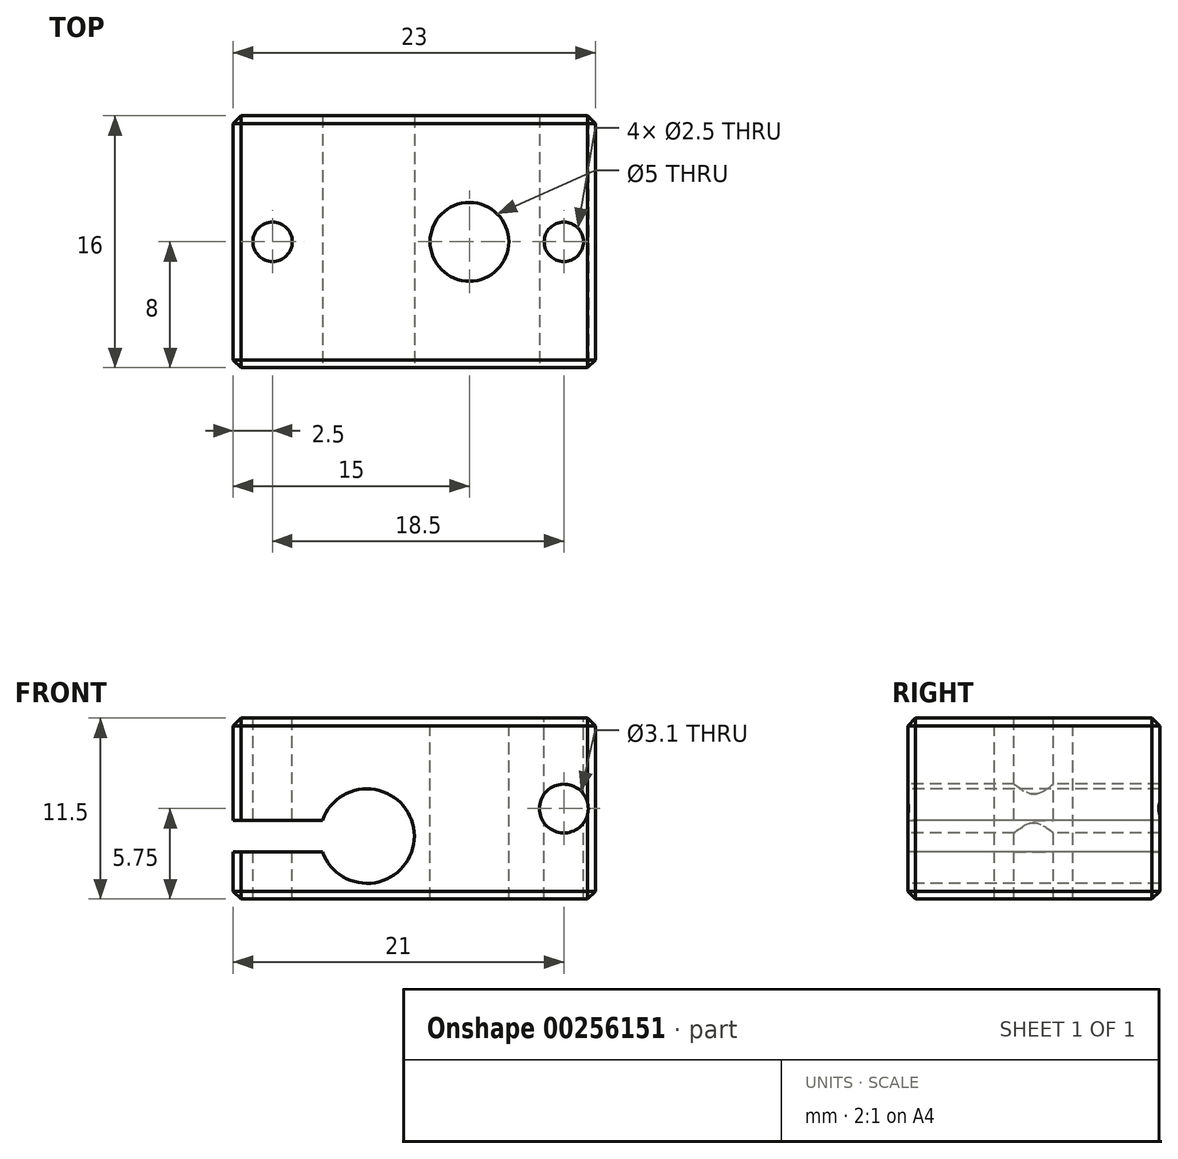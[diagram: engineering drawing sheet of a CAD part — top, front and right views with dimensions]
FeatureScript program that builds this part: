
annotation { "Feature Type Name" : "Feature", "Feature Type Description" : "" }
export const myFeature = defineFeature(function(context is Context, id is Id, definition is map)
    precondition{}
    {
        {
            var Q0;
            Q0=qCreatedBy(makeId("Front.planeOp"),FACE);
            var sketch = newSketch(context, id + "F0", { "sketchPlane" : qUnion([Q0])});
            skLineSegment(sketch, "E0.bottom", {"start": v(-11.5, 5.75) * mm, "end": v(11.5, 5.75) * mm});
            skLineSegment(sketch, "E0.top", {"start": v(-11.5, -5.75) * mm, "end": v(11.5, -5.75) * mm});
            skLineSegment(sketch, "E0.left", {"start": v(-11.5, 5.75) * mm, "end": v(-11.5, -5.75) * mm});
            skLineSegment(sketch, "E0.right", {"start": v(11.5, 5.75) * mm, "end": v(11.5, -5.75) * mm});
            skPoint(sketch, "E0.middle", {"position": v(0, 0) * mm});
            skSolve(sketch);
        }
        {
            var Q0;
            Q0=makeQuery(id+"F0.imprint","IMPRINT",FACE,{"disambiguationData":[TD([[makeQuery(id+"F0.imprint","IMPRINT",EDGE,{"derivedFrom":sQuery(id+"F0.wireOp",EDGE,"E0.bottom")}),-1.0]])]});
            extrude(context, id + "F1", {"entities" : qUnion([Q0]), "endBound" : BoundingType.SYMMETRIC, "depth" : 16 * mm});
        }
        {
            var Q0;
            Q0=makeQuery(id+"F1.opExtrude","CAP_FACE",FACE,{"disambiguationData":[OSD([sQuery(id+"F0.wireOp",EDGE,"E0.bottom"),sQuery(id+"F0.wireOp",EDGE,"E0.top"),sQuery(id+"F0.wireOp",EDGE,"E0.left"),sQuery(id+"F0.wireOp",EDGE,"E0.right")])],"isStart":false});
            var sketch = newSketch(context, id + "F2", { "sketchPlane" : qUnion([Q0])});
            skArc(sketch, "E1", {"start": v(-5.83, -2.75) * mm, "mid": v(0, -1.75) * mm, "end": v(-5.83, -0.75) * mm});
            skCircle(sketch, "E2", {"center": v(9.5, 0) * mm, "radius": 1.55 * mm});
            skLineSegment(sketch, "E3", {"start": v(-5.83, -2.75) * mm, "end": v(-11.5, -2.75) * mm});
            skLineSegment(sketch, "E4", {"start": v(-11.5, -2.75) * mm, "end": v(-11.5, -0.75) * mm});
            skLineSegment(sketch, "E5", {"start": v(-11.5, -0.75) * mm, "end": v(-5.83, -0.75) * mm});
            skSolve(sketch);
        }
        {
            var Q0;
            Q0 = qSketchRegion(id + "F2", true);
            extrude(context, id + "F3", {"entities" : qUnion([Q0]), "operationType" : NewBodyOperationType.REMOVE, "endBound" : BoundingType.UP_TO_NEXT, "oppositeDirection" : true, "depth" : 25 * mm});
        }
        {
            var Q0;
            Q0=makeQuery(id+"F1.opExtrude","SWEPT_FACE",FACE,{"disambiguationData":[OSD([sQuery(id+"F0.wireOp",EDGE,"E0.bottom")])]});
            var sketch = newSketch(context, id + "F4", { "sketchPlane" : qUnion([Q0])});
            skCircle(sketch, "E6", {"center": v(-9, 0) * mm, "radius": 1.25 * mm});
            skCircle(sketch, "E7", {"center": v(3.5, 0) * mm, "radius": 2.5 * mm});
            skCircle(sketch, "E8", {"center": v(9.5, 0) * mm, "radius": 1.25 * mm});
            skSolve(sketch);
        }
        {
            var Q0;
            Q0 = qSketchRegion(id + "F4", true);
            extrude(context, id + "F5", {"entities" : qUnion([Q0]), "operationType" : NewBodyOperationType.REMOVE, "endBound" : BoundingType.THROUGH_ALL, "oppositeDirection" : true, "depth" : 25 * mm});
        }
        {
            var Q0;
            Q0=makeQuery(id+"F1.opExtrude","CAP_EDGE",EDGE,{"disambiguationData":[OSD([sQuery(id+"F0.wireOp",EDGE,"E0.bottom")])],"isStart":false});
            var Q1;
            {var subQ0=sQuery(id+"F0.wireOp",EDGE,"E0.bottom");var subQ1=sQuery(id+"F0.wireOp",EDGE,"E0.left");Q1=makeQuery(id+"F3.boolean.opBoolean","SPLIT",EDGE,{"disambiguationData":[TD([makeQuery(id+"F1.opExtrude","SWEPT_FACE",FACE,{"disambiguationData":[OSD([subQ0])]})])],"derivedFrom":makeQuery(id+"F1.opExtrude","CAP_EDGE",EDGE,{"disambiguationData":[OSD([subQ1])],"isStart":false})});}
            var Q2;
            {var subQ0=sQuery(id+"F0.wireOp",EDGE,"E0.left");var subQ1=sQuery(id+"F0.wireOp",EDGE,"E0.top");Q2=makeQuery(id+"F3.boolean.opBoolean","SPLIT",EDGE,{"disambiguationData":[TD([makeQuery(id+"F1.opExtrude","SWEPT_FACE",FACE,{"disambiguationData":[OSD([subQ1])]})])],"derivedFrom":makeQuery(id+"F1.opExtrude","CAP_EDGE",EDGE,{"disambiguationData":[OSD([subQ0])],"isStart":false})});}
            var Q3;
            Q3=makeQuery(id+"F1.opExtrude","CAP_EDGE",EDGE,{"disambiguationData":[OSD([sQuery(id+"F0.wireOp",EDGE,"E0.top")])],"isStart":false});
            var Q4;
            Q4=makeQuery(id+"F1.opExtrude","SWEPT_EDGE",EDGE,{"disambiguationData":[OSD([sQuery(id+"F0.wireOp",EDGE,"E0.bottom"),sQuery(id+"F0.wireOp",EDGE,"E0.right")])]});
            var Q5;
            Q5=makeQuery(id+"F1.opExtrude","CAP_EDGE",EDGE,{"disambiguationData":[OSD([sQuery(id+"F0.wireOp",EDGE,"E0.right")])],"isStart":false});
            var Q6;
            Q6=makeQuery(id+"F1.opExtrude","SWEPT_EDGE",EDGE,{"disambiguationData":[OSD([sQuery(id+"F0.wireOp",EDGE,"E0.top"),sQuery(id+"F0.wireOp",EDGE,"E0.right")])]});
            var Q7;
            Q7=makeQuery(id+"F1.opExtrude","SWEPT_FACE",FACE,{"disambiguationData":[OSD([sQuery(id+"F0.wireOp",EDGE,"E0.right")])]});
            var Q8;
            Q8=makeQuery(id+"F1.opExtrude","CAP_EDGE",EDGE,{"disambiguationData":[OSD([sQuery(id+"F0.wireOp",EDGE,"E0.bottom")])],"isStart":true});
            var Q9;
            Q9=makeQuery(id+"F1.opExtrude","CAP_EDGE",EDGE,{"disambiguationData":[OSD([sQuery(id+"F0.wireOp",EDGE,"E0.top")])],"isStart":true});
            var Q10;
            {var subQ0=sQuery(id+"F0.wireOp",EDGE,"E0.bottom");var subQ1=sQuery(id+"F0.wireOp",EDGE,"E0.left");Q10=makeQuery(id+"F3.boolean.opBoolean","SPLIT",EDGE,{"disambiguationData":[TD([makeQuery(id+"F1.opExtrude","SWEPT_FACE",FACE,{"disambiguationData":[OSD([subQ0])]})])],"derivedFrom":makeQuery(id+"F1.opExtrude","CAP_EDGE",EDGE,{"disambiguationData":[OSD([subQ1])],"isStart":true})});}
            var Q11;
            {var subQ0=sQuery(id+"F0.wireOp",EDGE,"E0.left");var subQ1=sQuery(id+"F0.wireOp",EDGE,"E0.top");Q11=makeQuery(id+"F3.boolean.opBoolean","SPLIT",EDGE,{"disambiguationData":[TD([makeQuery(id+"F1.opExtrude","SWEPT_FACE",FACE,{"disambiguationData":[OSD([subQ1])]})])],"derivedFrom":makeQuery(id+"F1.opExtrude","CAP_EDGE",EDGE,{"disambiguationData":[OSD([subQ0])],"isStart":true})});}
            var Q12;
            Q12=makeQuery(id+"F1.opExtrude","SWEPT_EDGE",EDGE,{"disambiguationData":[OSD([sQuery(id+"F0.wireOp",EDGE,"E0.bottom"),sQuery(id+"F0.wireOp",EDGE,"E0.left")])]});
            var Q13;
            Q13=makeQuery(id+"F1.opExtrude","SWEPT_EDGE",EDGE,{"disambiguationData":[OSD([sQuery(id+"F0.wireOp",EDGE,"E0.top"),sQuery(id+"F0.wireOp",EDGE,"E0.left")])]});
            var Q14;
            Q14=makeQuery(id+"F3.boolean.opBoolean","COPY",EDGE,{"derivedFrom":makeQuery(id+"F3.opExtrude","CAP_EDGE",EDGE,{"disambiguationData":[OSD([sQuery(id+"F2.wireOp",EDGE,"E1")])],"isStart":false})});
            var Q15;
            Q15=makeQuery(id+"F3.boolean.opBoolean","COPY",EDGE,{"derivedFrom":makeQuery(id+"F3.opExtrude","CAP_EDGE",EDGE,{"disambiguationData":[OSD([sQuery(id+"F2.wireOp",EDGE,"E1")])],"isStart":true})});
            chamfer(context, id + "F6", {"entities" : qUnion([Q0, Q1, Q2, Q3, Q4, Q5, Q6, Q7, Q8, Q9, Q10, Q11, Q12, Q13, Q14, Q15]), "width" : 0.5 * mm, "tangentPropagation" : true});
        }
    });
